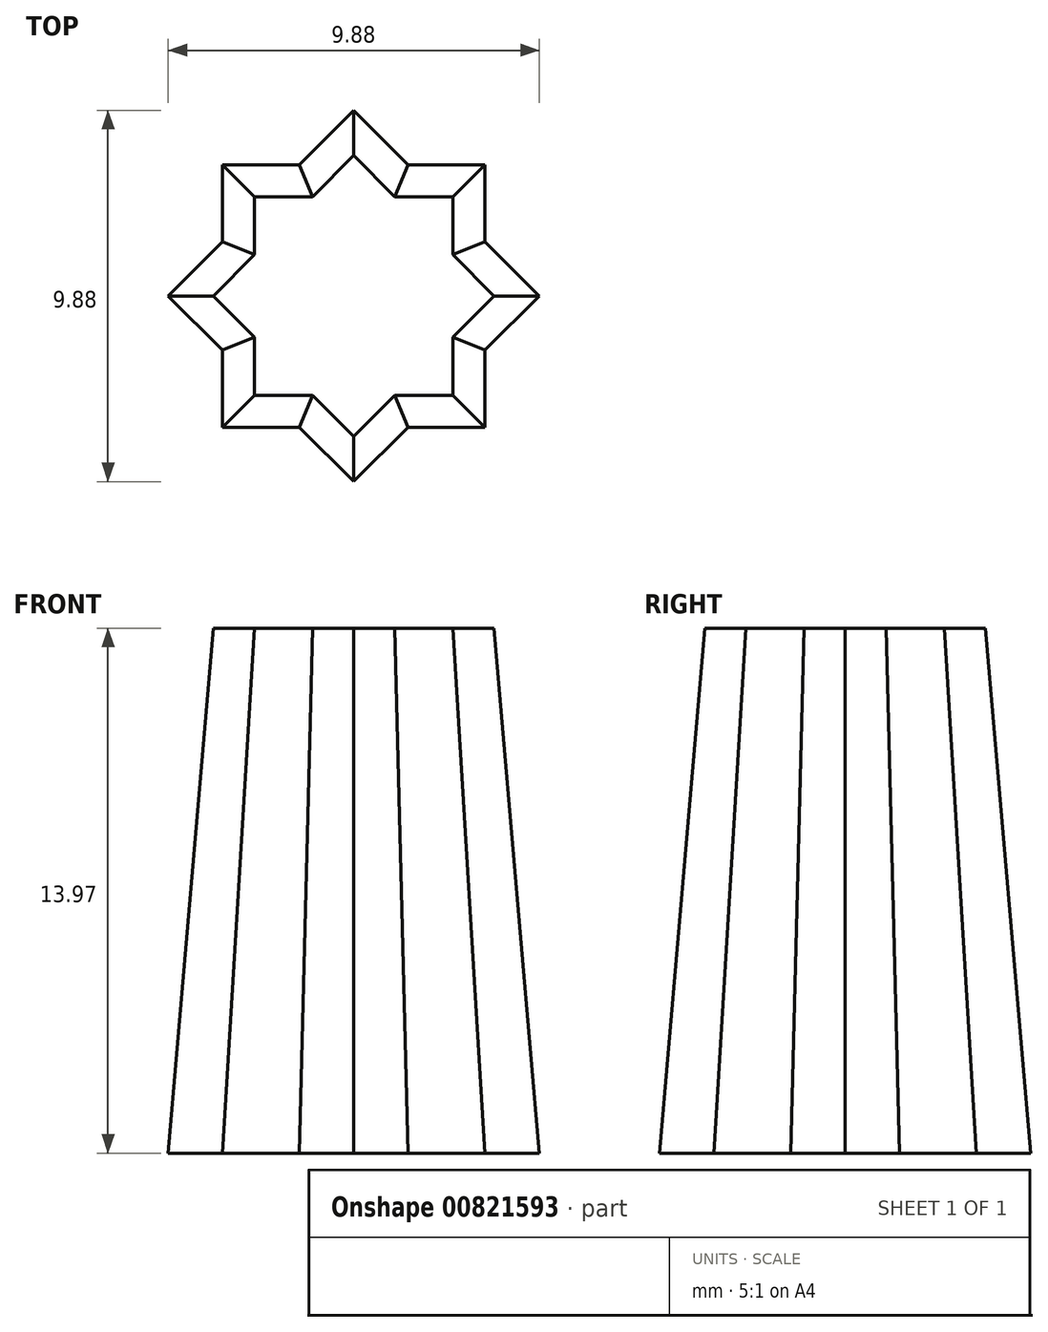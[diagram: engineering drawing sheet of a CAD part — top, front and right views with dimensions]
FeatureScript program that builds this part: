
annotation { "Feature Type Name" : "Feature", "Feature Type Description" : "" }
export const myFeature = defineFeature(function(context is Context, id is Id, definition is map)
    precondition{}
    {
        {
            var Q0;
            Q0=qCreatedBy(makeId("Top.planeOp"),FACE);
            var sketch = newSketch(context, id + "F0", { "sketchPlane" : qUnion([Q0])});
            skLineSegment(sketch, "E0.bottom", {"start": v(3.5, -3.5) * mm, "end": v(-3.5, -3.5) * mm});
            skLineSegment(sketch, "E0.top", {"start": v(3.5, 3.5) * mm, "end": v(-3.5, 3.5) * mm});
            skLineSegment(sketch, "E0.left", {"start": v(3.5, -3.5) * mm, "end": v(3.5, 3.5) * mm});
            skLineSegment(sketch, "E0.right", {"start": v(-3.5, -3.5) * mm, "end": v(-3.5, 3.5) * mm});
            skPoint(sketch, "E0.middle", {"position": v(0, 0) * mm});
            skLineSegment(sketch, "E1.bottom", {"start": v(4.94, 0) * mm, "end": v(0, -4.94) * mm});
            skLineSegment(sketch, "E1.top", {"start": v(0, 4.94) * mm, "end": v(-4.94, 0) * mm});
            skLineSegment(sketch, "E1.left", {"start": v(4.94, 0) * mm, "end": v(0, 4.94) * mm});
            skLineSegment(sketch, "E1.right", {"start": v(0, -4.94) * mm, "end": v(-4.94, 0) * mm});
            skLineSegment(sketch, "E2", {"start": v(-3.5, 1.45) * mm, "end": v(3.5, -1.45) * mm, "construction": true});
            skLineSegment(sketch, "E3", {"start": v(3.5, 1.45) * mm, "end": v(-3.5, -1.45) * mm, "construction": true});
            skLineSegment(sketch, "E4", {"start": v(1.45, 3.5) * mm, "end": v(-1.45, -3.5) * mm, "construction": true});
            skLineSegment(sketch, "E5", {"start": v(-1.45, 3.5) * mm, "end": v(1.45, -3.5) * mm, "construction": true});
            skCircle(sketch, "E6", {"center": v(0, 0) * mm, "radius": 3.68 * mm, "construction": true});
            skSolve(sketch);
        }
        {
            var Q0;
            {var subQ5=sQuery(id+"F0.wireOp",EDGE,"E1.bottom");var subQ13=sQuery(id+"F0.wireOp",EDGE,"E0.bottom");var subQ14=makeQuery(id+"F0.imprint","INTERSECT",VERTEX,{"derivedFrom":[subQ13,subQ5]});Q0=makeQuery(id+"F0.imprint","IMPRINT",FACE,{"disambiguationData":[TD([[makeQuery(id+"F0.imprint","IMPRINT",EDGE,{"disambiguationData":[TD([[subQ14,-1.0]])],"derivedFrom":subQ13}),-1.0]])]});}
            cPlane(context, id + "F1", {"entities" : qUnion([Q0]), "cplaneType" : CPlaneType.OFFSET, "offset" : 13.97 * mm, "width" : 152.4 * mm, "height" : 152.4 * mm});
        }
        {
            var Q0;
            Q0=qCreatedBy(id+"F1.planeOp",FACE);
            var sketch = newSketch(context, id + "F2", { "sketchPlane" : qUnion([Q0])});
            skLineSegment(sketch, "E7.bottom", {"start": v(2.64, -2.64) * mm, "end": v(-2.64, -2.64) * mm});
            skLineSegment(sketch, "E7.top", {"start": v(2.64, 2.64) * mm, "end": v(-2.64, 2.64) * mm});
            skLineSegment(sketch, "E7.left", {"start": v(2.64, -2.64) * mm, "end": v(2.64, 2.64) * mm});
            skLineSegment(sketch, "E7.right", {"start": v(-2.64, -2.64) * mm, "end": v(-2.64, 2.64) * mm});
            skPoint(sketch, "E7.middle", {"position": v(0, 0) * mm});
            skLineSegment(sketch, "E8.bottom", {"start": v(0, -3.74) * mm, "end": v(-3.74, 0) * mm});
            skLineSegment(sketch, "E8.top", {"start": v(3.74, 0) * mm, "end": v(0, 3.74) * mm});
            skLineSegment(sketch, "E8.left", {"start": v(0, -3.74) * mm, "end": v(3.74, 0) * mm});
            skLineSegment(sketch, "E8.right", {"start": v(-3.74, 0) * mm, "end": v(0, 3.74) * mm});
            skLineSegment(sketch, "E9", {"start": v(2.64, 2.64) * mm, "end": v(-2.64, -2.64) * mm, "construction": true});
            skSolve(sketch);
        }
        {
            var Q0;
            Q0=qSketchRegion(id+"F2",true);
            var Q1;
            Q1=qSketchRegion(id+"F0",true);
            loft(context, id + "F3", {"sheetProfilesArray" : [{ "sheetProfileEntities" : qUnion([Q0]) }, { "sheetProfileEntities" : qUnion([Q1]) }]});
        }
    });
